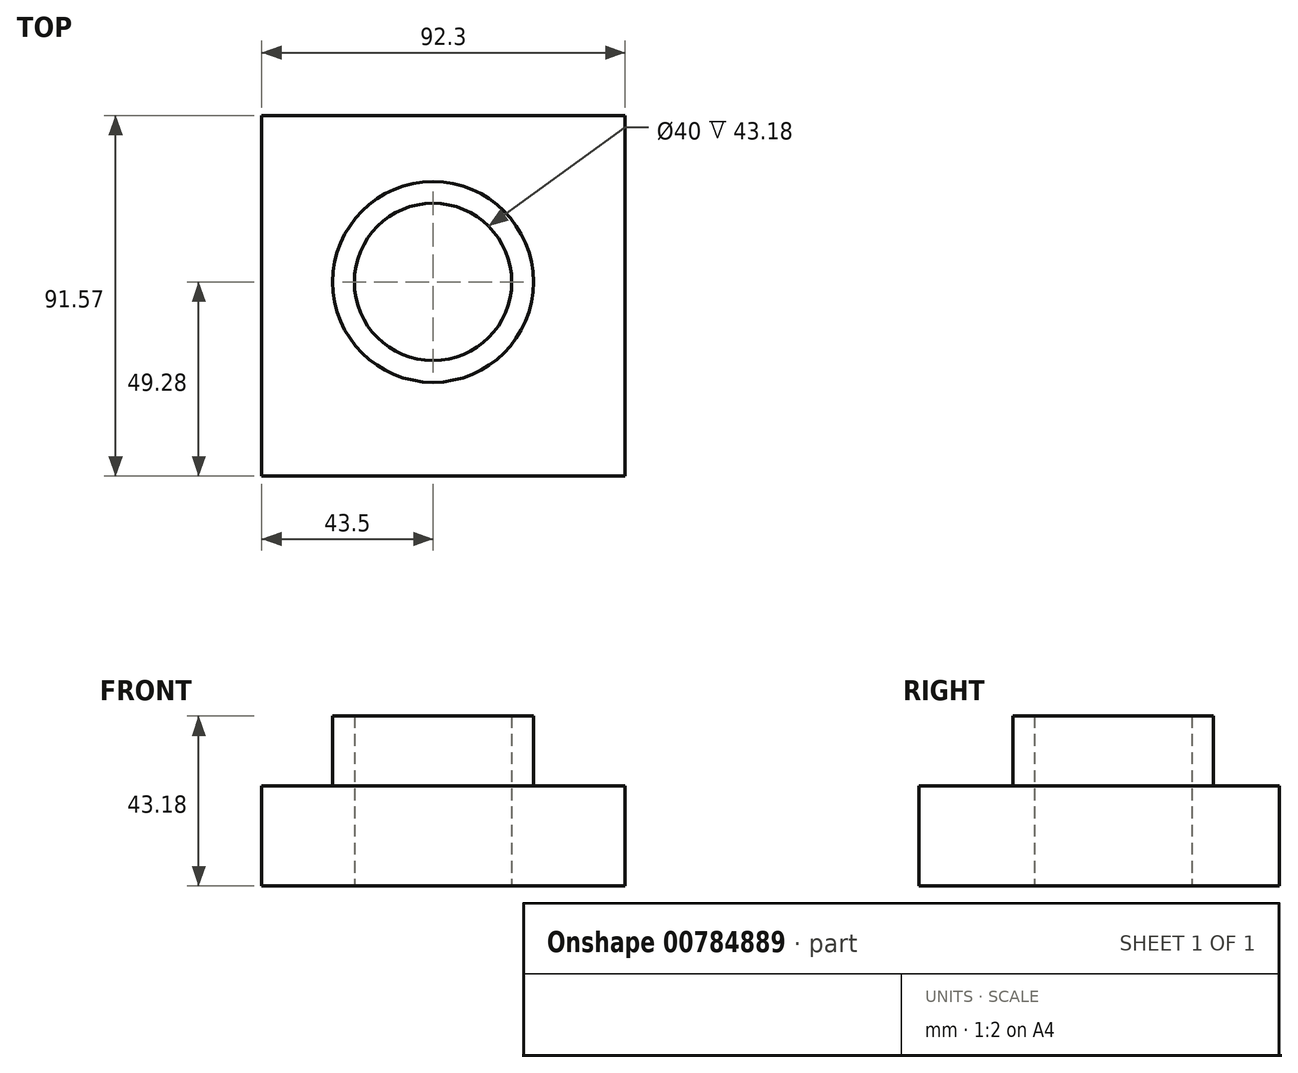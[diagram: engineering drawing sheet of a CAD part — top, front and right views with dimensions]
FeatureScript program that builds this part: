
annotation { "Feature Type Name" : "Feature", "Feature Type Description" : "" }
export const myFeature = defineFeature(function(context is Context, id is Id, definition is map)
    precondition{}
    {
        {
            var Q0;
            Q0=qCreatedBy(makeId("Top.planeOp"),FACE);
            var sketch = newSketch(context, id + "F0", { "sketchPlane" : qUnion([Q0])});
            skLineSegment(sketch, "E0.bottom", {"start": v(-43.5, 42.3) * mm, "end": v(48.8, 42.3) * mm});
            skLineSegment(sketch, "E0.top", {"start": v(-43.5, -49.28) * mm, "end": v(48.8, -49.28) * mm});
            skLineSegment(sketch, "E0.left", {"start": v(-43.5, 42.3) * mm, "end": v(-43.5, -49.28) * mm});
            skLineSegment(sketch, "E0.right", {"start": v(48.8, 42.3) * mm, "end": v(48.8, -49.28) * mm});
            skCircle(sketch, "E1", {"center": v(0, 0) * mm, "radius": 25.5 * mm});
            skCircle(sketch, "E2", {"center": v(0, 0) * mm, "radius": 20 * mm});
            skSolve(sketch);
        }
        {
            var Q0;
            Q0=makeQuery(id+"F0.imprint","IMPRINT",FACE,{"disambiguationData":[TD([[makeQuery(id+"F0.imprint","IMPRINT",EDGE,{"derivedFrom":sQuery(id+"F0.wireOp",EDGE,"E1")}),1.0]])]});
            extrude(context, id + "F1", {"entities" : qUnion([Q0]), "depth" : 43.18 * mm, "offsetDistance" : 25.4 * mm});
        }
        {
            var Q0;
            Q0=makeQuery(id+"F0.imprint","IMPRINT",FACE,{"disambiguationData":[TD([[makeQuery(id+"F0.imprint","IMPRINT",EDGE,{"derivedFrom":sQuery(id+"F0.wireOp",EDGE,"E0.bottom")}),-1.0]])]});
            extrude(context, id + "F2", {"entities" : qUnion([Q0]), "operationType" : NewBodyOperationType.ADD, "depth" : 25.4 * mm, "offsetDistance" : 25.4 * mm});
        }
    });
